# Revit family: Safety & Protection_Barrier_UltiGroup_Traffic Impact Barrier
name_source: partatom
category: Generic Models
revit_build: Autodesk Revit Architecture 2016 (Build: 20150220_1215(x64)
units: mm (PartAtom-declared; Revit-internal decimal feet)

## family parameters
Always vertical = Yes
Can host rebar = No
Cut with Voids When Loaded = No
OmniClass Number = 23.30.80.17.11
OmniClass Title = Impact Guard Rails
Part Type = Normal
Room Calculation Point = No
Round Connector Dimension = Use Diameter
Shared = No
Work Plane-Based = No

## types (6) — shared parameters
Barrier Yellow = Barrier
Base Plate thickness = 16 mm  [stored 0.0524934 ft]
Bolts = Bolts
Bottom Barrier = Yes
Fax = 07 846 2467
Manufacturer = UltiGroup
Model = Ulti Traffic Impact Barrier
Post Yellow = Post Yellow
Post cap = Post cap
Right Post = Yes
Send Message = http://ultigroup.co.nz
URL = www.ultigroup.co.nz
zero-valued in all types: InstallationGroup_ANZRS, ModifiedIssue_ANZRS

## per-type parameters (varying)
| type | Barrier Galvanised | Description | Left Post | Post Galvanised | Post height | Top Barrier |
| 470mm High - Yellow | Barrier | 470mm High Traffic Impact Barrier, Yellow powder coated Finish | Yes | Post Yellow | 470 mm  [stored 1.54199 ft] | No |
| 470mm High - Galvanised | Barrier Galvanised | 470mm High Traffic Impact Barrier, Galvanised Finish | Yes | Post Galvanised | 470 mm  [stored 1.54199 ft] | No |
| 1085mm High - Yellow | Barrier | 1085mm High Traffic Impact Barrier, Yellow powder coated Finish | Yes | Post Yellow | 1085 mm  [stored 3.55971 ft] | Yes |
| 1085mm High - Galvanised | Barrier Galvanised | 1085mm High Traffic Impact Barrier, Galvanised Finish | Yes | Post Galvanised | 1085 mm  [stored 3.55971 ft] | Yes |
| 470mm High - Galvanised 2 | Barrier Galvanised | 470mm High Traffic Impact Barrier, Galvanised Finish | No | Post Galvanised | 470 mm  [stored 1.54199 ft] | No |
| 1085mm High - Yellow 2 | Barrier | 1085mm High Traffic Impact Barrier, Yellow powder coated Finish | No | Post Yellow | 1085 mm  [stored 3.55971 ft] | Yes |

note: [stored X ft] marks values corroborated as IEEE doubles in the binary element streams (Revit-internal decimal feet)

## geometry (parser evidence)
native form markers: Blend x2, Sweep x2
no freeform markers — native parametric forms only
